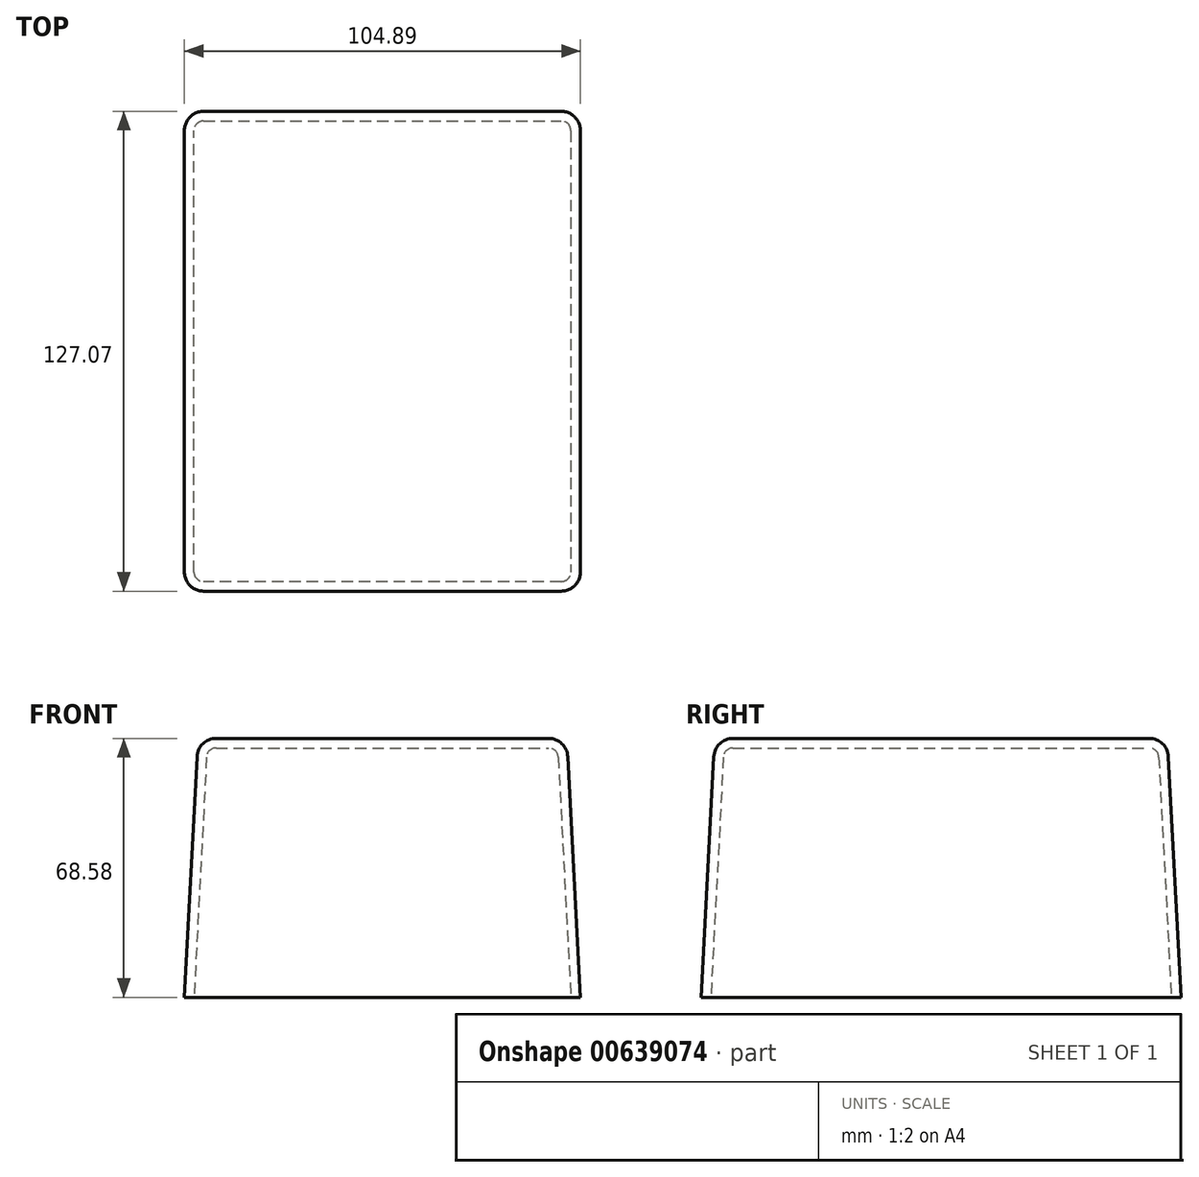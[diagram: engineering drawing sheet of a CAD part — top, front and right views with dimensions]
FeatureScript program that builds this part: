
annotation { "Feature Type Name" : "Feature", "Feature Type Description" : "" }
export const myFeature = defineFeature(function(context is Context, id is Id, definition is map)
    precondition{}
    {
        {
            var Q0;
            Q0=qCreatedBy(makeId("Top.planeOp"),FACE);
            var sketch = newSketch(context, id + "F0", { "sketchPlane" : qUnion([Q0])});
            skLineSegment(sketch, "E0.bottom", {"start": v(0, 0) * mm, "end": v(104.9, 0) * mm});
            skLineSegment(sketch, "E0.top", {"start": v(0, 127.07) * mm, "end": v(104.9, 127.07) * mm});
            skLineSegment(sketch, "E0.left", {"start": v(0, 0) * mm, "end": v(0, 127.07) * mm});
            skLineSegment(sketch, "E0.right", {"start": v(104.9, 0) * mm, "end": v(104.9, 127.07) * mm});
            skSolve(sketch);
        }
        {
            var Q0;
            Q0=makeQuery(id+"F0.imprint","IMPRINT",FACE,{"disambiguationData":[TD([[makeQuery(id+"F0.imprint","IMPRINT",EDGE,{"derivedFrom":sQuery(id+"F0.wireOp",EDGE,"E0.bottom")}),1.0]])]});
            extrude(context, id + "F1", {"entities" : qUnion([Q0]), "depth" : 68.58 * mm, "offsetDistance" : 25.4 * mm, "hasDraft" : true, "draftAngle" : 3 * degree, "draftPullDirection" : true});
        }
        {
            var Q0;
            Q0=makeQuery(id+"F1.opExtrude","SWEPT_EDGE",EDGE,{"disambiguationData":[OSD([sQuery(id+"F0.wireOp",EDGE,"E0.bottom"),sQuery(id+"F0.wireOp",EDGE,"E0.right")])]});
            var Q1;
            Q1=makeQuery(id+"F1.opExtrude","SWEPT_EDGE",EDGE,{"disambiguationData":[OSD([sQuery(id+"F0.wireOp",EDGE,"E0.top"),sQuery(id+"F0.wireOp",EDGE,"E0.right")])]});
            var Q2;
            Q2=makeQuery(id+"F1.opExtrude","SWEPT_EDGE",EDGE,{"disambiguationData":[OSD([sQuery(id+"F0.wireOp",EDGE,"E0.top"),sQuery(id+"F0.wireOp",EDGE,"E0.left")])]});
            var Q3;
            Q3=makeQuery(id+"F1.opExtrude","SWEPT_EDGE",EDGE,{"disambiguationData":[OSD([sQuery(id+"F0.wireOp",EDGE,"E0.bottom"),sQuery(id+"F0.wireOp",EDGE,"E0.left")])]});
            var Q4;
            Q4=makeQuery(id+"F1.opExtrude","CAP_FACE",FACE,{"disambiguationData":[OSD([sQuery(id+"F0.wireOp",EDGE,"E0.bottom"),sQuery(id+"F0.wireOp",EDGE,"E0.top"),sQuery(id+"F0.wireOp",EDGE,"E0.left"),sQuery(id+"F0.wireOp",EDGE,"E0.right")])],"isStart":false});
            fillet(context, id + "F2", {"entities" : qUnion([Q0, Q1, Q2, Q3, Q4]), "radius" : 5.08 * mm, "tangentPropagation" : true, "allowEdgeOverflow" : false});
        }
        {
            var Q0;
            Q0=makeQuery(id+"F1.opExtrude","CAP_FACE",FACE,{"disambiguationData":[OSD([sQuery(id+"F0.wireOp",EDGE,"E0.bottom"),sQuery(id+"F0.wireOp",EDGE,"E0.top"),sQuery(id+"F0.wireOp",EDGE,"E0.left"),sQuery(id+"F0.wireOp",EDGE,"E0.right")])],"isStart":true});
            shell(context, id + "F3", {"entities" : qUnion([Q0]), "thickness" : 2.54 * mm});
        }
    });
